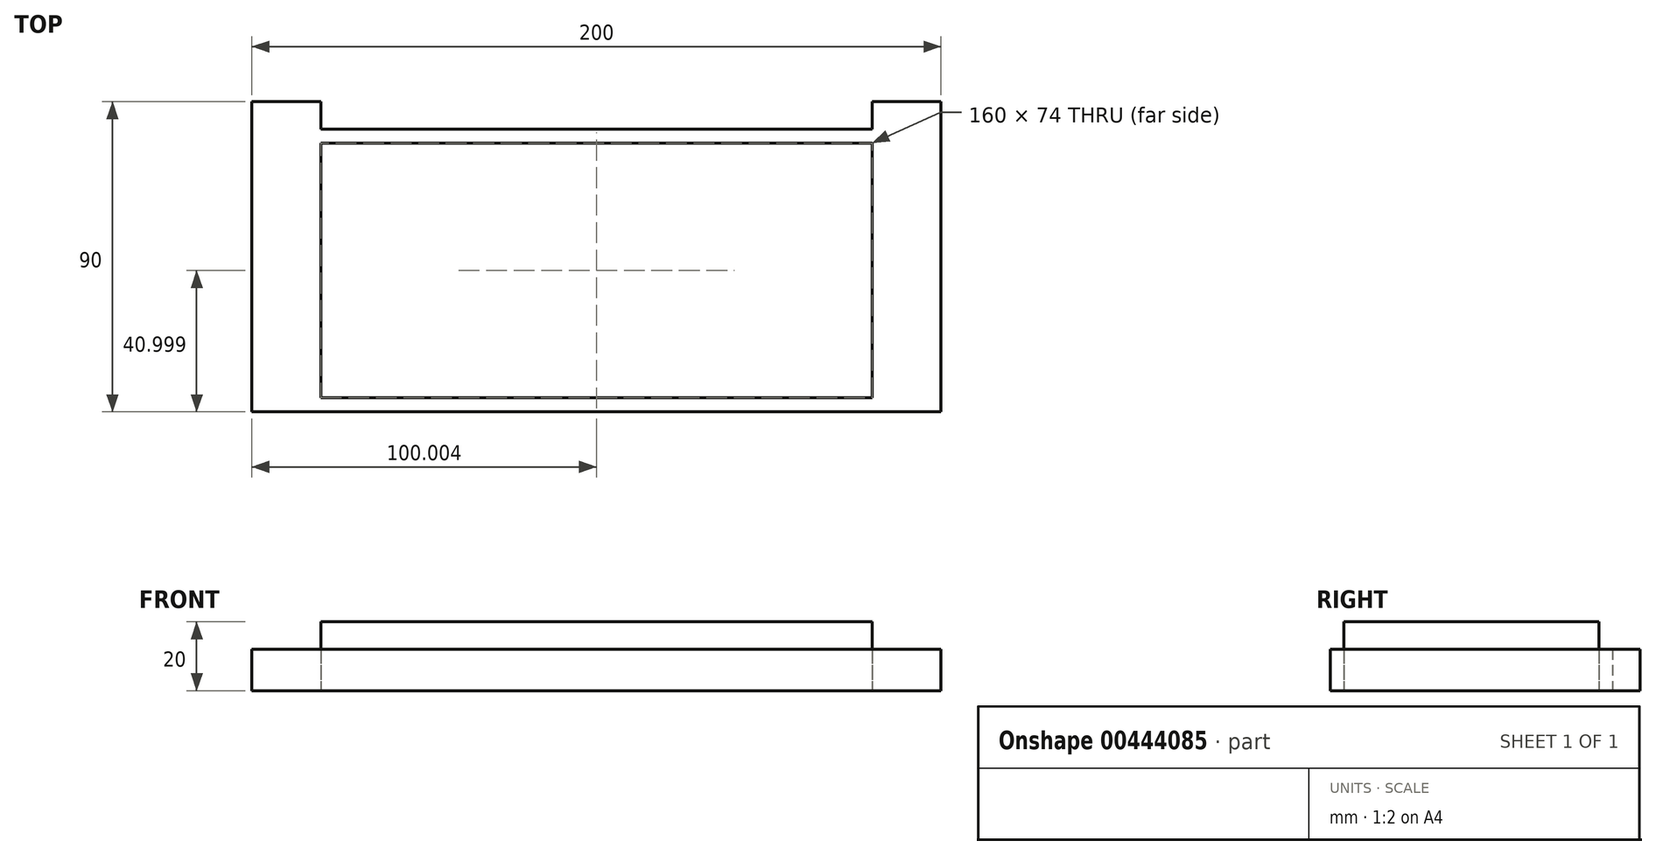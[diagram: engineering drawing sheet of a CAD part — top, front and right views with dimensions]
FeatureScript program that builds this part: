
annotation { "Feature Type Name" : "Feature", "Feature Type Description" : "" }
export const myFeature = defineFeature(function(context is Context, id is Id, definition is map)
    precondition{}
    {
        {
            var Q0;
            Q0=qCreatedBy(makeId("Top.planeOp"),FACE);
            var sketch = newSketch(context, id + "F0", { "sketchPlane" : qUnion([Q0])});
            skLineSegment(sketch, "E0.bottom", {"start": v(-97.74, 43.53) * mm, "end": v(102.26, 43.53) * mm});
            skLineSegment(sketch, "E0.top", {"start": v(-97.74, -46.47) * mm, "end": v(102.26, -46.47) * mm});
            skLineSegment(sketch, "E0.left", {"start": v(-97.74, 43.53) * mm, "end": v(-97.74, -46.47) * mm});
            skLineSegment(sketch, "E0.right", {"start": v(102.26, 43.53) * mm, "end": v(102.26, -46.47) * mm});
            skLineSegment(sketch, "E1.bottom", {"start": v(-77.74, 43.53) * mm, "end": v(82.26, 43.53) * mm});
            skLineSegment(sketch, "E1.top", {"start": v(-77.74, 35.53) * mm, "end": v(82.26, 35.53) * mm});
            skLineSegment(sketch, "E1.left", {"start": v(-77.74, 43.53) * mm, "end": v(-77.74, 35.53) * mm});
            skLineSegment(sketch, "E1.right", {"start": v(82.26, 43.53) * mm, "end": v(82.26, 35.53) * mm});
            skLineSegment(sketch, "E2.bottom", {"start": v(-77.74, 31.53) * mm, "end": v(82.26, 31.53) * mm});
            skLineSegment(sketch, "E2.top", {"start": v(-77.74, -42.47) * mm, "end": v(82.26, -42.47) * mm});
            skLineSegment(sketch, "E2.left", {"start": v(-77.74, 31.53) * mm, "end": v(-77.74, -42.47) * mm});
            skLineSegment(sketch, "E2.right", {"start": v(82.26, 31.53) * mm, "end": v(82.26, -42.47) * mm});
            skSolve(sketch);
        }
        {
            var Q0;
            Q0=makeQuery(id+"F0.imprint","IMPRINT",FACE,{"disambiguationData":[TD([[makeQuery(id+"F0.imprint","IMPRINT",EDGE,{"derivedFrom":sQuery(id+"F0.wireOp",EDGE,"E1.bottom")}),-1.0]])]});
            var Q1;
            Q1=makeQuery(id+"F0.imprint","IMPRINT",FACE,{"disambiguationData":[TD([[makeQuery(id+"F0.imprint","IMPRINT",EDGE,{"derivedFrom":sQuery(id+"F0.wireOp",EDGE,"E2.bottom")}),-1.0]])]});
            extrude(context, id + "F1", {"entities" : qUnion([Q0, Q1]), "depth" : 20 * mm});
        }
        {
            var Q0;
            Q0=makeQuery(id+"F0.imprint","IMPRINT",FACE,{"disambiguationData":[TD([[makeQuery(id+"F0.imprint","IMPRINT",EDGE,{"derivedFrom":sQuery(id+"F0.wireOp",EDGE,"E0.top")}),1.0]])]});
            extrude(context, id + "F2", {"entities" : qUnion([Q0]), "depth" : 12 * mm});
        }
    });
